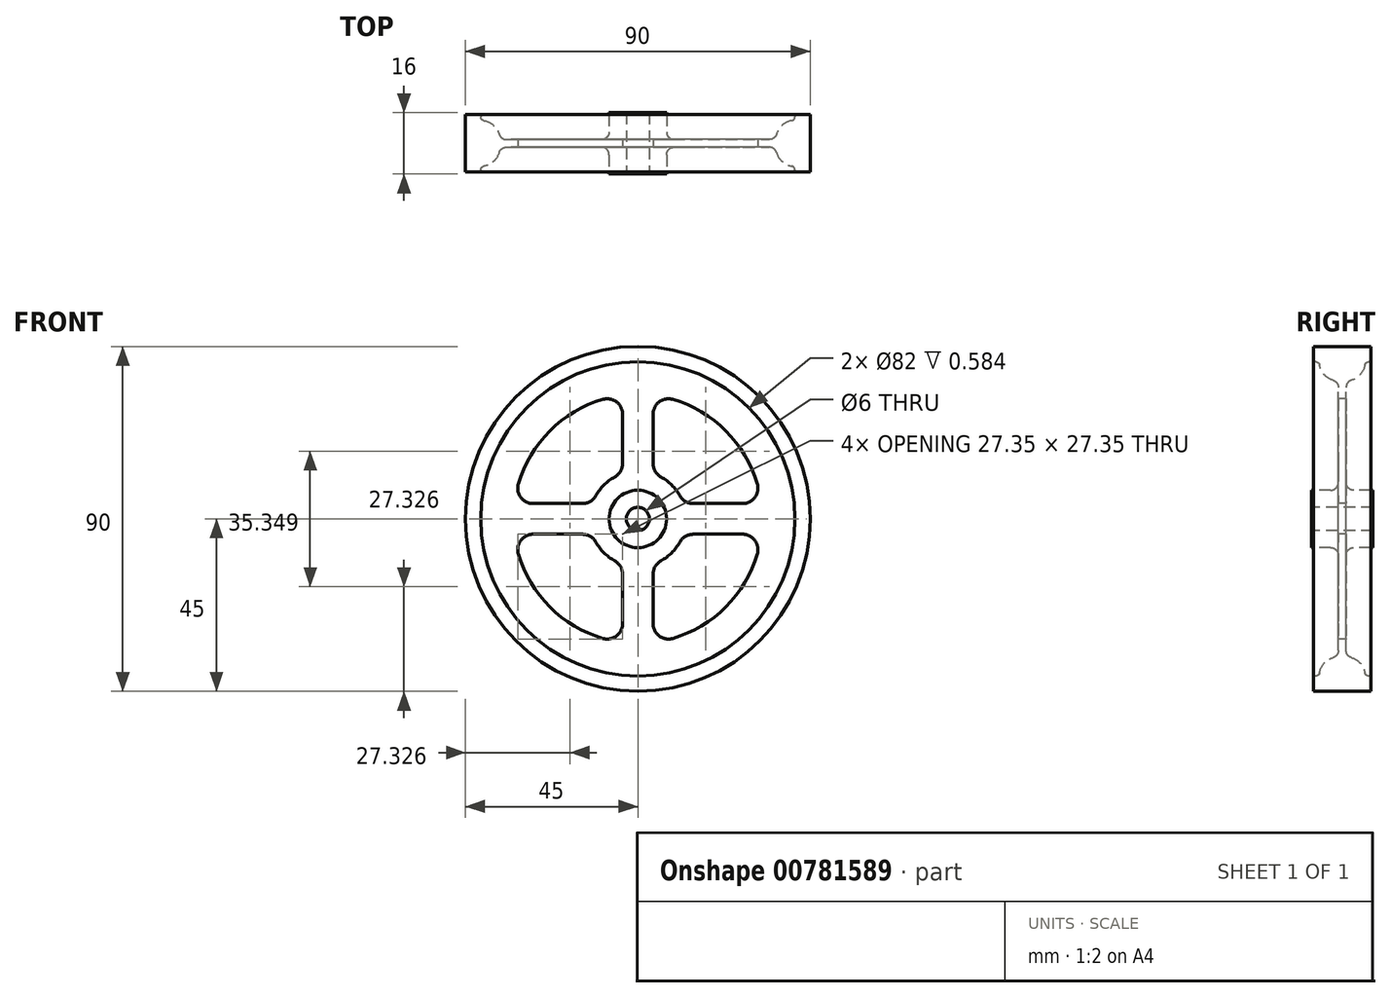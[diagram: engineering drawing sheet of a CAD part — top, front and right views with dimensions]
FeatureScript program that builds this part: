
annotation { "Feature Type Name" : "Feature", "Feature Type Description" : "" }
export const myFeature = defineFeature(function(context is Context, id is Id, definition is map)
    precondition{}
    {
        {
            var Q0;
            Q0=qCreatedBy(makeId("Right.planeOp"),FACE);
            var sketch = newSketch(context, id + "F0", { "sketchPlane" : qUnion([Q0])});
            skLineSegment(sketch, "E0", {"start": v(-8, 3) * mm, "end": v(-8, 0) * mm, "construction": true});
            skLineSegment(sketch, "E1", {"start": v(-8, 0) * mm, "end": v(8, 0) * mm, "construction": true});
            skLineSegment(sketch, "E2", {"start": v(8, 0) * mm, "end": v(8, 3) * mm, "construction": true});
            skLineSegment(sketch, "E3", {"start": v(-8, 3) * mm, "end": v(8, 3) * mm});
            skLineSegment(sketch, "E4", {"start": v(-8, 7.5) * mm, "end": v(-8, 3) * mm});
            skLineSegment(sketch, "E5", {"start": v(8, 7.5) * mm, "end": v(8, 3) * mm});
            skLineSegment(sketch, "E6", {"start": v(0, 0) * mm, "end": v(0, 45) * mm, "construction": true});
            skLineSegment(sketch, "E7", {"start": v(-7.5, 45) * mm, "end": v(7.5, 45) * mm});
            skLineSegment(sketch, "E8", {"start": v(-7.5, 45) * mm, "end": v(-7.5, 41) * mm});
            skLineSegment(sketch, "E9", {"start": v(-7.5, 41) * mm, "end": v(-6.92, 41) * mm});
            skLineSegment(sketch, "E10", {"start": v(-1, 41) * mm, "end": v(-1, 36) * mm, "construction": true});
            skLineSegment(sketch, "E11", {"start": v(-3, 7.5) * mm, "end": v(-8, 7.5) * mm});
            skArc(sketch, "E12", {"start": v(-5.93, 40.17) * mm, "mid": v(-4.74, 37.69) * mm, "end": v(-2.43, 36.2) * mm});
            skLineSegment(sketch, "E13", {"start": v(-6, 41) * mm, "end": v(-1, 41) * mm, "construction": true});
            skLineSegment(sketch, "E14", {"start": v(-1, 34.3) * mm, "end": v(-1, 9.5) * mm});
            skPoint(sketch, "E15.visualSharp", {"position": v(-1, 36) * mm});
            skArc(sketch, "E15.filletArc", {"start": v(-1, 34.3) * mm, "mid": v(-1.4, 35.49) * mm, "end": v(-2.43, 36.2) * mm});
            skPoint(sketch, "E16.visualSharp", {"position": v(-1, 7.5) * mm});
            skArc(sketch, "E16.filletArc", {"start": v(-3, 7.5) * mm, "mid": v(-1.59, 8.09) * mm, "end": v(-1, 9.5) * mm});
            skPoint(sketch, "E17.visualSharp", {"position": v(-6, 41) * mm});
            skArc(sketch, "E17.filletArc", {"start": v(-5.93, 40.17) * mm, "mid": v(-6.27, 40.76) * mm, "end": v(-6.92, 41) * mm});
            skLineSegment(sketch, "E18.MirrorCS", {"start": v(7.5, 45) * mm, "end": v(7.5, 41) * mm});
            skArc(sketch, "E19.MirrorCS", {"start": v(5.93, 40.17) * mm, "mid": v(4.74, 37.69) * mm, "end": v(2.43, 36.2) * mm});
            skLineSegment(sketch, "E20.MirrorCS", {"start": v(1, 34.3) * mm, "end": v(1, 9.5) * mm});
            skLineSegment(sketch, "E21.MirrorCS", {"start": v(3, 7.5) * mm, "end": v(8, 7.5) * mm});
            skArc(sketch, "E22.MirrorCS", {"start": v(3, 7.5) * mm, "mid": v(1.59, 8.09) * mm, "end": v(1, 9.5) * mm});
            skLineSegment(sketch, "E23.MirrorCS", {"start": v(7.5, 41) * mm, "end": v(6.92, 41) * mm});
            skArc(sketch, "E24.MirrorCS", {"start": v(5.93, 40.17) * mm, "mid": v(6.27, 40.76) * mm, "end": v(6.92, 41) * mm});
            skArc(sketch, "E25.MirrorCS", {"start": v(1, 34.3) * mm, "mid": v(1.4, 35.49) * mm, "end": v(2.43, 36.2) * mm});
            skSolve(sketch);
        }
        {
            var Q0;
            Q0 = qSketchRegion(id + "F0", true);
            var Q1;
            Q1=sQuery(id+"F0.wireOp",EDGE,"E1");
            revolve(context, id + "F1", {"surfaceOperationType" : NewSurfaceOperationType.NEW, "entities" : qUnion([Q0]), "axis" : qUnion([Q1]), "revolveType" : RevolveType.FULL});
        }
        {
            var Q0;
            Q0=makeQuery(id+"F1.opRevolve","SWEPT_FACE",FACE,{"disambiguationData":[OSD([sQuery(id+"F0.wireOp",EDGE,"E14")])]});
            var sketch = newSketch(context, id + "F2", { "sketchPlane" : qUnion([Q0])});
            skArc(sketch, "E26", {"start": v(-10.93, 6.06) * mm, "mid": v(-8.84, 8.84) * mm, "end": v(-6.06, 10.93) * mm});
            skLineSegment(sketch, "E27", {"start": v(0, 0) * mm, "end": v(0, 45) * mm, "construction": true});
            skLineSegment(sketch, "E28", {"start": v(0, 0) * mm, "end": v(-45, 0) * mm, "construction": true});
            skArc(sketch, "E29", {"start": v(-31.2, 9.12) * mm, "mid": v(-22.98, 22.98) * mm, "end": v(-9.12, 31.2) * mm});
            skLineSegment(sketch, "E30", {"start": v(-4, 14.43) * mm, "end": v(-4, 27.35) * mm});
            skLineSegment(sketch, "E31", {"start": v(-14.43, 4) * mm, "end": v(-27.35, 4) * mm});
            skPoint(sketch, "E32.visualSharp", {"position": v(-32.25, 4) * mm});
            skArc(sketch, "E32.filletArc", {"start": v(-31.2, 9.12) * mm, "mid": v(-30.56, 5.6) * mm, "end": v(-27.35, 4) * mm});
            skPoint(sketch, "E33.visualSharp", {"position": v(-11.84, 4) * mm});
            skArc(sketch, "E33.filletArc", {"start": v(-14.43, 4) * mm, "mid": v(-12.4, 4.55) * mm, "end": v(-10.93, 6.06) * mm});
            skPoint(sketch, "E34.visualSharp", {"position": v(-4, 11.84) * mm});
            skArc(sketch, "E34.filletArc", {"start": v(-6.06, 10.93) * mm, "mid": v(-4.55, 12.4) * mm, "end": v(-4, 14.43) * mm});
            skPoint(sketch, "E35.visualSharp", {"position": v(-4, 32.25) * mm});
            skArc(sketch, "E35.filletArc", {"start": v(-4, 27.35) * mm, "mid": v(-5.6, 30.56) * mm, "end": v(-9.12, 31.2) * mm});
            skArc(sketch, "E36.1.0", {"start": v(-6.06, -10.93) * mm, "mid": v(-8.84, -8.84) * mm, "end": v(-10.93, -6.06) * mm});
            skLineSegment(sketch, "E36.1.1", {"start": v(-14.43, -4) * mm, "end": v(-27.35, -4) * mm});
            skArc(sketch, "E36.1.2", {"start": v(-9.12, -31.2) * mm, "mid": v(-22.98, -22.98) * mm, "end": v(-31.2, -9.12) * mm});
            skLineSegment(sketch, "E36.1.3", {"start": v(-4, -14.43) * mm, "end": v(-4, -27.35) * mm});
            skArc(sketch, "E36.1.4", {"start": v(-9.12, -31.2) * mm, "mid": v(-5.6, -30.56) * mm, "end": v(-4, -27.35) * mm});
            skArc(sketch, "E36.1.5", {"start": v(-27.35, -4) * mm, "mid": v(-30.56, -5.6) * mm, "end": v(-31.2, -9.12) * mm});
            skArc(sketch, "E36.1.6", {"start": v(-4, -14.43) * mm, "mid": v(-4.55, -12.4) * mm, "end": v(-6.06, -10.93) * mm});
            skArc(sketch, "E36.1.7", {"start": v(-10.93, -6.06) * mm, "mid": v(-12.4, -4.55) * mm, "end": v(-14.43, -4) * mm});
            skArc(sketch, "E36.2.0", {"start": v(10.93, -6.06) * mm, "mid": v(8.84, -8.84) * mm, "end": v(6.06, -10.93) * mm});
            skLineSegment(sketch, "E36.2.1", {"start": v(4, -14.43) * mm, "end": v(4, -27.35) * mm});
            skArc(sketch, "E36.2.2", {"start": v(31.2, -9.12) * mm, "mid": v(22.98, -22.98) * mm, "end": v(9.12, -31.2) * mm});
            skLineSegment(sketch, "E36.2.3", {"start": v(14.43, -4) * mm, "end": v(27.35, -4) * mm});
            skArc(sketch, "E36.2.4", {"start": v(31.2, -9.12) * mm, "mid": v(30.56, -5.6) * mm, "end": v(27.35, -4) * mm});
            skArc(sketch, "E36.2.5", {"start": v(4, -27.35) * mm, "mid": v(5.6, -30.56) * mm, "end": v(9.12, -31.2) * mm});
            skArc(sketch, "E36.2.6", {"start": v(14.43, -4) * mm, "mid": v(12.4, -4.55) * mm, "end": v(10.93, -6.06) * mm});
            skArc(sketch, "E36.2.7", {"start": v(6.06, -10.93) * mm, "mid": v(4.55, -12.4) * mm, "end": v(4, -14.43) * mm});
            skArc(sketch, "E36.3.0", {"start": v(6.06, 10.93) * mm, "mid": v(8.84, 8.84) * mm, "end": v(10.93, 6.06) * mm});
            skLineSegment(sketch, "E36.3.1", {"start": v(14.43, 4) * mm, "end": v(27.35, 4) * mm});
            skArc(sketch, "E36.3.2", {"start": v(9.12, 31.2) * mm, "mid": v(22.98, 22.98) * mm, "end": v(31.2, 9.12) * mm});
            skLineSegment(sketch, "E36.3.3", {"start": v(4, 14.43) * mm, "end": v(4, 27.35) * mm});
            skArc(sketch, "E36.3.4", {"start": v(9.12, 31.2) * mm, "mid": v(5.6, 30.56) * mm, "end": v(4, 27.35) * mm});
            skArc(sketch, "E36.3.5", {"start": v(27.35, 4) * mm, "mid": v(30.56, 5.6) * mm, "end": v(31.2, 9.12) * mm});
            skArc(sketch, "E36.3.6", {"start": v(4, 14.43) * mm, "mid": v(4.55, 12.4) * mm, "end": v(6.06, 10.93) * mm});
            skArc(sketch, "E36.3.7", {"start": v(10.93, 6.06) * mm, "mid": v(12.4, 4.55) * mm, "end": v(14.43, 4) * mm});
            skSolve(sketch);
        }
        {
            var Q0;
            Q0 = qSketchRegion(id + "F2", true);
            extrude(context, id + "F3", {"entities" : qUnion([Q0]), "operationType" : NewBodyOperationType.REMOVE, "oppositeDirection" : true, "depth" : 25 * mm, "offsetDistance" : 25 * mm});
        }
    });
